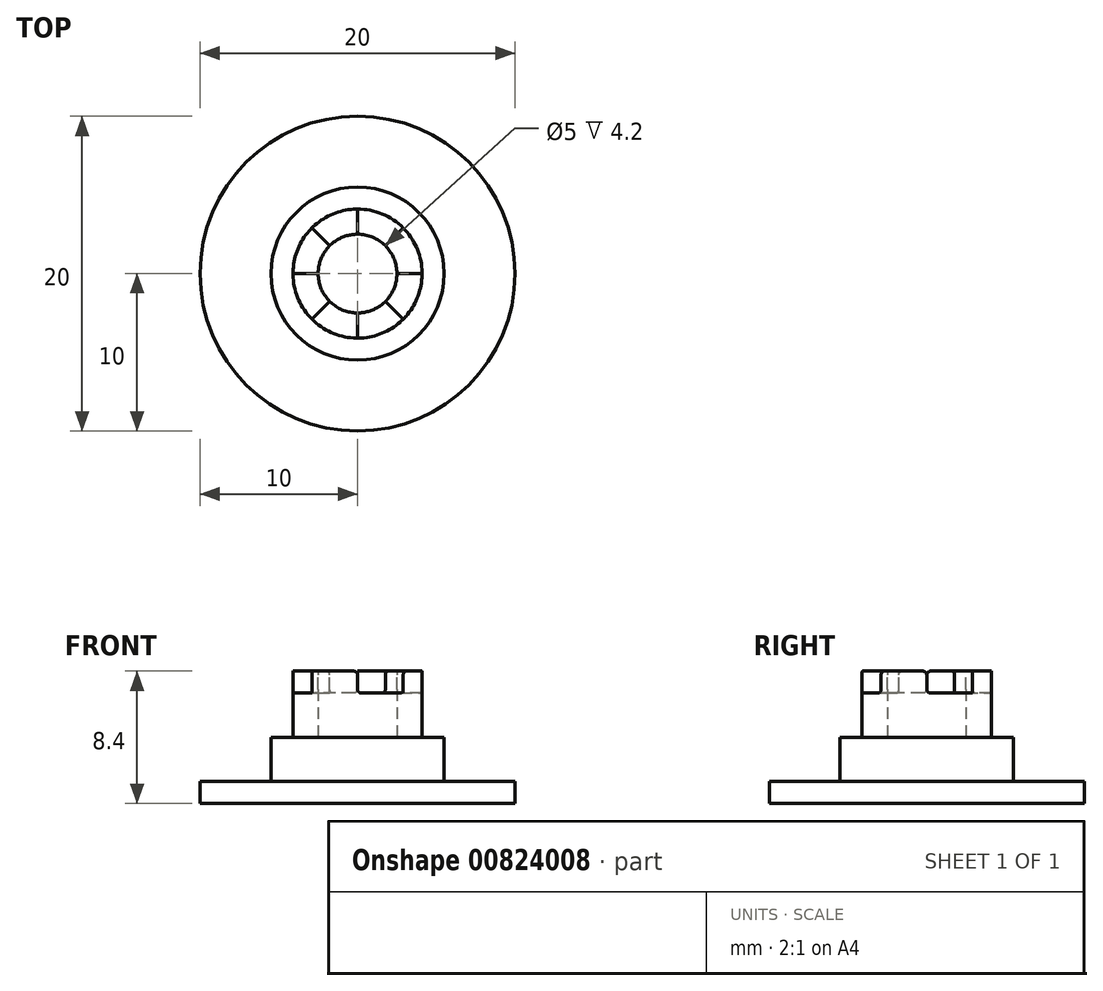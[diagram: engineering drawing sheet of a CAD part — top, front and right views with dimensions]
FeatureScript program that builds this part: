
annotation { "Feature Type Name" : "Feature", "Feature Type Description" : "" }
export const myFeature = defineFeature(function(context is Context, id is Id, definition is map)
    precondition{}
    {
        {
            var Q0;
            Q0=qCreatedBy(makeId("Top.planeOp"),FACE);
            var sketch = newSketch(context, id + "F0", { "sketchPlane" : qUnion([Q0])});
            skCircle(sketch, "E0", {"center": v(0, 0) * mm, "radius": 10 * mm});
            skSolve(sketch);
        }
        {
            var Q0;
            Q0=makeQuery(id+"F0.imprint","IMPRINT",FACE,{"disambiguationData":[TD([[makeQuery(id+"F0.imprint","IMPRINT",EDGE,{"derivedFrom":sQuery(id+"F0.wireOp",EDGE,"E0")}),1.0]])]});
            extrude(context, id + "F1", {"entities" : qUnion([Q0]), "depth" : 1.4 * mm, "offsetDistance" : 25 * mm});
        }
        {
            var Q0;
            Q0=makeQuery(id+"F1.opExtrude","CAP_FACE",FACE,{"disambiguationData":[OSD([sQuery(id+"F0.wireOp",EDGE,"E0")])],"isStart":false});
            var sketch = newSketch(context, id + "F2", { "sketchPlane" : qUnion([Q0])});
            skCircle(sketch, "E1", {"center": v(0, 0) * mm, "radius": 5.5 * mm});
            skSolve(sketch);
        }
        {
            var Q0;
            Q0=makeQuery(id+"F2.imprint","IMPRINT",FACE,{"disambiguationData":[TD([[makeQuery(id+"F2.imprint","IMPRINT",EDGE,{"derivedFrom":sQuery(id+"F2.wireOp",EDGE,"E1")}),1.0]])]});
            extrude(context, id + "F3", {"entities" : qUnion([Q0]), "operationType" : NewBodyOperationType.ADD, "depth" : 2.8 * mm, "offsetDistance" : 25 * mm});
        }
        {
            var Q0;
            Q0=makeQuery(id+"F3.opExtrude","CAP_FACE",FACE,{"disambiguationData":[OSD([sQuery(id+"F2.wireOp",EDGE,"E1")])],"isStart":false});
            var sketch = newSketch(context, id + "F4", { "sketchPlane" : qUnion([Q0])});
            skCircle(sketch, "E2", {"center": v(0, 0) * mm, "radius": 4.1 * mm});
            skCircle(sketch, "E3", {"center": v(0, 0) * mm, "radius": 2.5 * mm});
            skSolve(sketch);
        }
        {
            var Q0;
            Q0=makeQuery(id+"F4.imprint","IMPRINT",FACE,{"disambiguationData":[TD([[makeQuery(id+"F4.imprint","IMPRINT",EDGE,{"derivedFrom":sQuery(id+"F4.wireOp",EDGE,"E2")}),1.0]])]});
            extrude(context, id + "F5", {"entities" : qUnion([Q0]), "operationType" : NewBodyOperationType.ADD, "depth" : 4.2 * mm, "offsetDistance" : 25 * mm});
        }
        {
            var Q0;
            Q0=makeQuery(id+"F5.opExtrude","CAP_FACE",FACE,{"disambiguationData":[OSD([sQuery(id+"F4.wireOp",EDGE,"E2"),sQuery(id+"F4.wireOp",EDGE,"E3")])],"isStart":false});
            var sketch = newSketch(context, id + "F6", { "sketchPlane" : qUnion([Q0])});
            skLineSegment(sketch, "E4", {"start": v(0, -6.34) * mm, "end": v(0, 6.71) * mm});
            skLineSegment(sketch, "E5", {"start": v(-5.83, 0) * mm, "end": v(5.83, 0) * mm});
            skLineSegment(sketch, "E6", {"start": v(-5.41, -5.41) * mm, "end": v(5.41, 5.41) * mm});
            skLineSegment(sketch, "E7", {"start": v(-3.72, 3.72) * mm, "end": v(3.72, -3.72) * mm});
            skSolve(sketch);
        }
        {
            var Q0;
            {var subQ0=sQuery(id+"F6.wireOp",EDGE,"E4");var subQ1=makeQuery(id+"F5.opExtrude","CAP_EDGE",EDGE,{"disambiguationData":[OSD([sQuery(id+"F4.wireOp",EDGE,"E2")])],"isStart":false});var subQ2=makeQuery(id+"F6.imprint","INTERSECT",VERTEX,{"disambiguationData":[OD(1.0)],"derivedFrom":[subQ1,subQ0]});Q0=makeQuery(id+"F6.imprint","IMPRINT",FACE,{"disambiguationData":[TD([[makeQuery(id+"F6.imprint","IMPRINT",EDGE,{"disambiguationData":[TD([[subQ2,1.0]])],"derivedFrom":subQ0}),1.0]])]});}
            var Q1;
            {var subQ0=sQuery(id+"F6.wireOp",EDGE,"E5");var subQ1=makeQuery(id+"F5.opExtrude","CAP_EDGE",EDGE,{"disambiguationData":[OSD([sQuery(id+"F4.wireOp",EDGE,"E2")])],"isStart":false});var subQ2=makeQuery(id+"F6.imprint","INTERSECT",VERTEX,{"disambiguationData":[OD(1.0)],"derivedFrom":[subQ1,subQ0]});Q1=makeQuery(id+"F6.imprint","IMPRINT",FACE,{"disambiguationData":[TD([[makeQuery(id+"F6.imprint","IMPRINT",EDGE,{"disambiguationData":[TD([[subQ2,1.0]])],"derivedFrom":subQ0}),1.0]])]});}
            var Q2;
            {var subQ0=sQuery(id+"F6.wireOp",EDGE,"E4");var subQ1=makeQuery(id+"F5.opExtrude","CAP_EDGE",EDGE,{"disambiguationData":[OSD([sQuery(id+"F4.wireOp",EDGE,"E2")])],"isStart":false});var subQ2=makeQuery(id+"F6.imprint","INTERSECT",VERTEX,{"disambiguationData":[OD(0.0)],"derivedFrom":[subQ1,subQ0]});Q2=makeQuery(id+"F6.imprint","IMPRINT",FACE,{"disambiguationData":[TD([[makeQuery(id+"F6.imprint","IMPRINT",EDGE,{"disambiguationData":[TD([[subQ2,-1.0]])],"derivedFrom":subQ0}),-1.0]])]});}
            var Q3;
            {var subQ0=sQuery(id+"F6.wireOp",EDGE,"E5");var subQ1=makeQuery(id+"F5.opExtrude","CAP_EDGE",EDGE,{"disambiguationData":[OSD([sQuery(id+"F4.wireOp",EDGE,"E2")])],"isStart":false});var subQ2=makeQuery(id+"F6.imprint","INTERSECT",VERTEX,{"disambiguationData":[OD(0.0)],"derivedFrom":[subQ1,subQ0]});Q3=makeQuery(id+"F6.imprint","IMPRINT",FACE,{"disambiguationData":[TD([[makeQuery(id+"F6.imprint","IMPRINT",EDGE,{"disambiguationData":[TD([[subQ2,-1.0]])],"derivedFrom":subQ0}),-1.0]])]});}
            extrude(context, id + "F7", {"entities" : qUnion([Q0, Q1, Q2, Q3]), "operationType" : NewBodyOperationType.REMOVE, "oppositeDirection" : true, "depth" : 1.4 * mm, "offsetDistance" : 25 * mm});
        }
        {
            var Q0;
            {var subQ0=sQuery(id+"F6.wireOp",EDGE,"E5");Q0=makeQuery(id+"F7.boolean.opBoolean","COPY",EDGE,{"derivedFrom":makeQuery(id+"F7.opExtrude","CAP_EDGE",EDGE,{"disambiguationData":[OSD([subQ0]),TDD([makeQuery(id+"F6.imprint","IMPRINT",EDGE,{"disambiguationData":[TD([[makeQuery(id+"F6.imprint","INTERSECT",VERTEX,{"disambiguationData":[OD(0.0)],"derivedFrom":[makeQuery(id+"F5.opExtrude","CAP_EDGE",EDGE,{"disambiguationData":[OSD([sQuery(id+"F4.wireOp",EDGE,"E2")])],"isStart":false}),subQ0]}),-1.0]])],"derivedFrom":subQ0})])],"isStart":true})});}
            var Q1;
            {var subQ0=sQuery(id+"F6.wireOp",EDGE,"E7");Q1=makeQuery(id+"F7.boolean.opBoolean","COPY",EDGE,{"derivedFrom":makeQuery(id+"F7.opExtrude","CAP_EDGE",EDGE,{"disambiguationData":[OSD([subQ0]),TDD([makeQuery(id+"F6.imprint","IMPRINT",EDGE,{"disambiguationData":[TD([[makeQuery(id+"F6.imprint","INTERSECT",VERTEX,{"disambiguationData":[OD(0.0)],"derivedFrom":[makeQuery(id+"F5.opExtrude","CAP_EDGE",EDGE,{"disambiguationData":[OSD([sQuery(id+"F4.wireOp",EDGE,"E2")])],"isStart":false}),subQ0]}),-1.0]])],"derivedFrom":subQ0})])],"isStart":true})});}
            var Q2;
            {var subQ0=sQuery(id+"F6.wireOp",EDGE,"E4");Q2=makeQuery(id+"F7.boolean.opBoolean","COPY",EDGE,{"derivedFrom":makeQuery(id+"F7.opExtrude","CAP_EDGE",EDGE,{"disambiguationData":[OSD([subQ0]),TDD([makeQuery(id+"F6.imprint","IMPRINT",EDGE,{"disambiguationData":[TD([[makeQuery(id+"F6.imprint","INTERSECT",VERTEX,{"disambiguationData":[OD(1.0)],"derivedFrom":[makeQuery(id+"F5.opExtrude","CAP_EDGE",EDGE,{"disambiguationData":[OSD([sQuery(id+"F4.wireOp",EDGE,"E2")])],"isStart":false}),subQ0]}),1.0]])],"derivedFrom":subQ0})])],"isStart":true})});}
            var Q3;
            {var subQ0=sQuery(id+"F6.wireOp",EDGE,"E6");Q3=makeQuery(id+"F7.boolean.opBoolean","COPY",EDGE,{"derivedFrom":makeQuery(id+"F7.opExtrude","CAP_EDGE",EDGE,{"disambiguationData":[OSD([subQ0]),TDD([makeQuery(id+"F6.imprint","IMPRINT",EDGE,{"disambiguationData":[TD([[makeQuery(id+"F6.imprint","INTERSECT",VERTEX,{"disambiguationData":[OD(1.0)],"derivedFrom":[makeQuery(id+"F5.opExtrude","CAP_EDGE",EDGE,{"disambiguationData":[OSD([sQuery(id+"F4.wireOp",EDGE,"E2")])],"isStart":false}),subQ0]}),1.0]])],"derivedFrom":subQ0})])],"isStart":true})});}
            var Q4;
            {var subQ0=sQuery(id+"F6.wireOp",EDGE,"E5");Q4=makeQuery(id+"F7.boolean.opBoolean","COPY",EDGE,{"derivedFrom":makeQuery(id+"F7.opExtrude","CAP_EDGE",EDGE,{"disambiguationData":[OSD([subQ0]),TDD([makeQuery(id+"F6.imprint","IMPRINT",EDGE,{"disambiguationData":[TD([[makeQuery(id+"F6.imprint","INTERSECT",VERTEX,{"disambiguationData":[OD(1.0)],"derivedFrom":[makeQuery(id+"F5.opExtrude","CAP_EDGE",EDGE,{"disambiguationData":[OSD([sQuery(id+"F4.wireOp",EDGE,"E2")])],"isStart":false}),subQ0]}),1.0]])],"derivedFrom":subQ0})])],"isStart":true})});}
            var Q5;
            {var subQ0=sQuery(id+"F6.wireOp",EDGE,"E7");Q5=makeQuery(id+"F7.boolean.opBoolean","COPY",EDGE,{"derivedFrom":makeQuery(id+"F7.opExtrude","CAP_EDGE",EDGE,{"disambiguationData":[OSD([subQ0]),TDD([makeQuery(id+"F6.imprint","IMPRINT",EDGE,{"disambiguationData":[TD([[makeQuery(id+"F6.imprint","INTERSECT",VERTEX,{"disambiguationData":[OD(1.0)],"derivedFrom":[makeQuery(id+"F5.opExtrude","CAP_EDGE",EDGE,{"disambiguationData":[OSD([sQuery(id+"F4.wireOp",EDGE,"E2")])],"isStart":false}),subQ0]}),1.0]])],"derivedFrom":subQ0})])],"isStart":true})});}
            var Q6;
            {var subQ0=sQuery(id+"F6.wireOp",EDGE,"E4");Q6=makeQuery(id+"F7.boolean.opBoolean","COPY",EDGE,{"derivedFrom":makeQuery(id+"F7.opExtrude","CAP_EDGE",EDGE,{"disambiguationData":[OSD([subQ0]),TDD([makeQuery(id+"F6.imprint","IMPRINT",EDGE,{"disambiguationData":[TD([[makeQuery(id+"F6.imprint","INTERSECT",VERTEX,{"disambiguationData":[OD(0.0)],"derivedFrom":[makeQuery(id+"F5.opExtrude","CAP_EDGE",EDGE,{"disambiguationData":[OSD([sQuery(id+"F4.wireOp",EDGE,"E2")])],"isStart":false}),subQ0]}),-1.0]])],"derivedFrom":subQ0})])],"isStart":true})});}
            var Q7;
            {var subQ0=sQuery(id+"F6.wireOp",EDGE,"E6");Q7=makeQuery(id+"F7.boolean.opBoolean","COPY",EDGE,{"derivedFrom":makeQuery(id+"F7.opExtrude","CAP_EDGE",EDGE,{"disambiguationData":[OSD([subQ0]),TDD([makeQuery(id+"F6.imprint","IMPRINT",EDGE,{"disambiguationData":[TD([[makeQuery(id+"F6.imprint","INTERSECT",VERTEX,{"disambiguationData":[OD(0.0)],"derivedFrom":[makeQuery(id+"F5.opExtrude","CAP_EDGE",EDGE,{"disambiguationData":[OSD([sQuery(id+"F4.wireOp",EDGE,"E2")])],"isStart":false}),subQ0]}),-1.0]])],"derivedFrom":subQ0})])],"isStart":true})});}
            var Q8;
            {var subQ0=sQuery(id+"F6.wireOp",EDGE,"E5");Q8=makeQuery(id+"F7.boolean.opBoolean","COPY",EDGE,{"derivedFrom":makeQuery(id+"F7.opExtrude","CAP_EDGE",EDGE,{"disambiguationData":[OSD([subQ0]),TDD([makeQuery(id+"F6.imprint","IMPRINT",EDGE,{"disambiguationData":[TD([[makeQuery(id+"F6.imprint","INTERSECT",VERTEX,{"disambiguationData":[OD(0.0)],"derivedFrom":[makeQuery(id+"F5.opExtrude","CAP_EDGE",EDGE,{"disambiguationData":[OSD([sQuery(id+"F4.wireOp",EDGE,"E2")])],"isStart":false}),subQ0]}),-1.0]])],"derivedFrom":subQ0})])],"isStart":false})});}
            var Q9;
            {var subQ0=sQuery(id+"F6.wireOp",EDGE,"E4");Q9=makeQuery(id+"F7.boolean.opBoolean","COPY",EDGE,{"derivedFrom":makeQuery(id+"F7.opExtrude","CAP_EDGE",EDGE,{"disambiguationData":[OSD([subQ0]),TDD([makeQuery(id+"F6.imprint","IMPRINT",EDGE,{"disambiguationData":[TD([[makeQuery(id+"F6.imprint","INTERSECT",VERTEX,{"disambiguationData":[OD(0.0)],"derivedFrom":[makeQuery(id+"F5.opExtrude","CAP_EDGE",EDGE,{"disambiguationData":[OSD([sQuery(id+"F4.wireOp",EDGE,"E2")])],"isStart":false}),subQ0]}),-1.0]])],"derivedFrom":subQ0})])],"isStart":false})});}
            var Q10;
            {var subQ0=sQuery(id+"F6.wireOp",EDGE,"E7");Q10=makeQuery(id+"F7.boolean.opBoolean","COPY",EDGE,{"derivedFrom":makeQuery(id+"F7.opExtrude","CAP_EDGE",EDGE,{"disambiguationData":[OSD([subQ0]),TDD([makeQuery(id+"F6.imprint","IMPRINT",EDGE,{"disambiguationData":[TD([[makeQuery(id+"F6.imprint","INTERSECT",VERTEX,{"disambiguationData":[OD(1.0)],"derivedFrom":[makeQuery(id+"F5.opExtrude","CAP_EDGE",EDGE,{"disambiguationData":[OSD([sQuery(id+"F4.wireOp",EDGE,"E2")])],"isStart":false}),subQ0]}),1.0]])],"derivedFrom":subQ0})])],"isStart":false})});}
            var Q11;
            {var subQ0=sQuery(id+"F6.wireOp",EDGE,"E5");Q11=makeQuery(id+"F7.boolean.opBoolean","COPY",EDGE,{"derivedFrom":makeQuery(id+"F7.opExtrude","CAP_EDGE",EDGE,{"disambiguationData":[OSD([subQ0]),TDD([makeQuery(id+"F6.imprint","IMPRINT",EDGE,{"disambiguationData":[TD([[makeQuery(id+"F6.imprint","INTERSECT",VERTEX,{"disambiguationData":[OD(1.0)],"derivedFrom":[makeQuery(id+"F5.opExtrude","CAP_EDGE",EDGE,{"disambiguationData":[OSD([sQuery(id+"F4.wireOp",EDGE,"E2")])],"isStart":false}),subQ0]}),1.0]])],"derivedFrom":subQ0})])],"isStart":false})});}
            var Q12;
            {var subQ0=sQuery(id+"F6.wireOp",EDGE,"E6");Q12=makeQuery(id+"F7.boolean.opBoolean","COPY",EDGE,{"derivedFrom":makeQuery(id+"F7.opExtrude","CAP_EDGE",EDGE,{"disambiguationData":[OSD([subQ0]),TDD([makeQuery(id+"F6.imprint","IMPRINT",EDGE,{"disambiguationData":[TD([[makeQuery(id+"F6.imprint","INTERSECT",VERTEX,{"disambiguationData":[OD(1.0)],"derivedFrom":[makeQuery(id+"F5.opExtrude","CAP_EDGE",EDGE,{"disambiguationData":[OSD([sQuery(id+"F4.wireOp",EDGE,"E2")])],"isStart":false}),subQ0]}),1.0]])],"derivedFrom":subQ0})])],"isStart":false})});}
            var Q13;
            {var subQ0=sQuery(id+"F6.wireOp",EDGE,"E7");Q13=makeQuery(id+"F7.boolean.opBoolean","COPY",EDGE,{"derivedFrom":makeQuery(id+"F7.opExtrude","CAP_EDGE",EDGE,{"disambiguationData":[OSD([subQ0]),TDD([makeQuery(id+"F6.imprint","IMPRINT",EDGE,{"disambiguationData":[TD([[makeQuery(id+"F6.imprint","INTERSECT",VERTEX,{"disambiguationData":[OD(0.0)],"derivedFrom":[makeQuery(id+"F5.opExtrude","CAP_EDGE",EDGE,{"disambiguationData":[OSD([sQuery(id+"F4.wireOp",EDGE,"E2")])],"isStart":false}),subQ0]}),-1.0]])],"derivedFrom":subQ0})])],"isStart":false})});}
            var Q14;
            {var subQ0=sQuery(id+"F6.wireOp",EDGE,"E4");Q14=makeQuery(id+"F7.boolean.opBoolean","COPY",EDGE,{"derivedFrom":makeQuery(id+"F7.opExtrude","CAP_EDGE",EDGE,{"disambiguationData":[OSD([subQ0]),TDD([makeQuery(id+"F6.imprint","IMPRINT",EDGE,{"disambiguationData":[TD([[makeQuery(id+"F6.imprint","INTERSECT",VERTEX,{"disambiguationData":[OD(1.0)],"derivedFrom":[makeQuery(id+"F5.opExtrude","CAP_EDGE",EDGE,{"disambiguationData":[OSD([sQuery(id+"F4.wireOp",EDGE,"E2")])],"isStart":false}),subQ0]}),1.0]])],"derivedFrom":subQ0})])],"isStart":false})});}
            var Q15;
            {var subQ0=sQuery(id+"F6.wireOp",EDGE,"E6");Q15=makeQuery(id+"F7.boolean.opBoolean","COPY",EDGE,{"derivedFrom":makeQuery(id+"F7.opExtrude","CAP_EDGE",EDGE,{"disambiguationData":[OSD([subQ0]),TDD([makeQuery(id+"F6.imprint","IMPRINT",EDGE,{"disambiguationData":[TD([[makeQuery(id+"F6.imprint","INTERSECT",VERTEX,{"disambiguationData":[OD(0.0)],"derivedFrom":[makeQuery(id+"F5.opExtrude","CAP_EDGE",EDGE,{"disambiguationData":[OSD([sQuery(id+"F4.wireOp",EDGE,"E2")])],"isStart":false}),subQ0]}),-1.0]])],"derivedFrom":subQ0})])],"isStart":false})});}
            fillet(context, id + "F8", {"entities" : qUnion([Q0, Q1, Q2, Q3, Q4, Q5, Q6, Q7, Q8, Q9, Q10, Q11, Q12, Q13, Q14, Q15]), "radius" : 0.25 * mm, "tangentPropagation" : true, "allowEdgeOverflow" : false});
        }
    });
